# Revit family: Hand_Dryer-Wall_Mounted-Bobrick-InstaDry-B-7125
name_source: partatom
category: Electrical Fixtures
revit_build: Autodesk Revit 2014 (Build: 20130308_1515(x64)
units: mm (PartAtom-declared; Revit-internal decimal feet)

## types (1)
- B-7125
    115V AC, 12 Amp, 50/60 Hz, 202 Watts, cULus Listed and CE marked. = Yes
    208–240-V, 5.5-6.3 Amp, 50/60 Hz, 213 Watts, cULus Listed and CE marked. = No
    ADA Compliant = Yes
    Assembly Code = E1010
    Default Elevation = 44"
    Description = InstaDry Series Surface-Mounted Automatic Hand Dryer
    Height = 10 7/8"
    Installation Type = Surface-Mounted
    Length = 3 7/8"
    Manufacturer = Bobrick
    Material = Stainless Steel-Bobrick-304-Satin finish
    Model = B-7125
    Price = Prices may vary. Please consult Manufacturer Representative for most up-to-date price list.
    Product Page URL = http://bobrick.com
    Specification = Surface-mounted high-speed hand dryer shall have an energy consumption of only 200 watts. Unit shall have 18-gauge (1.2mm) thick Type-304 stainless steel cover with #4 satin finish vertical grain. The slim profile cover shall project no more than 3 7/8" (98mm) from the finished face of wall to comply with accessible design guidelines (including ADAAG in the U.S.A.) and have a dry time of less than 12 seconds. Dryer shall be universal, to accommodate voltages between 110-240V. Dryer shall be secured to concealed mounting bracket with vandal-resistant screws. Electronic sensor automatically turns dryer on when hands are held under air-outlet opening and across path of sensor. Dryer turns off automatically when hands are removed. Sensor automatically shuts dryer off approximately 85 seconds after dryer turns on if an inanimate object is placed across air-outlet opening. After object is removed, electronic sensor automatically resets itself and dryer operates normally. Unit is cULus listed and is CE marked. Dryer has a limited 5-year warranty on all parts.
    URL = http://www.bobrick.com
    Voltage = 115 V
    Warranty Information = 5 Year Limited Warranty
    Watts = 202 W
    Width = 12 5/8"

## geometry (parser evidence)
native form markers: Sweep x2
no freeform markers — native parametric forms only
